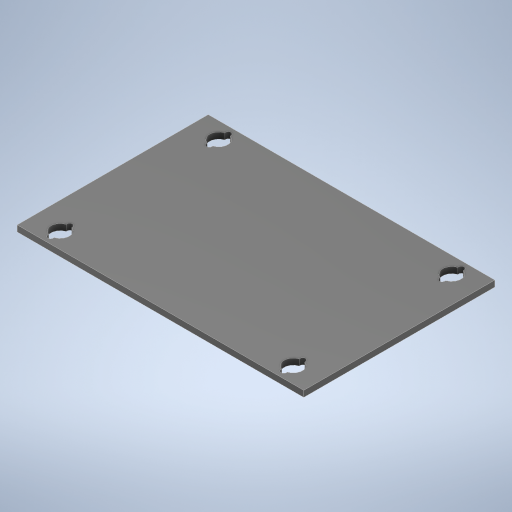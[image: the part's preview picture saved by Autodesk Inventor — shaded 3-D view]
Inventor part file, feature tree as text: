
AUTODESK INVENTOR PART (.ipt)
format: ipt  version: 2024.2 (Build 282272000, 272)  size: 255,488 bytes
history: native  units: mm
features: extrude x1, sketch x1
ambient origin geometry x8: Origin, YZ Plane, XZ Plane, XY Plane, X Axis, Y Axis, Z Axis, Center Point
bodies: Solid1 (feature_tree)
feature tree (2):
  extrude  "Extrusion1"  Depth=75.0mm
  sketch  "Sketch1"  dims[d0=50.0mm d1=75.0mm d2=4.8mm d4=1.5mm d6=14.0mm d7=1.6mm d8=0.0mm d9=61.0mm d10=41.5mm d11=6.5mm d12=1.0mm]
